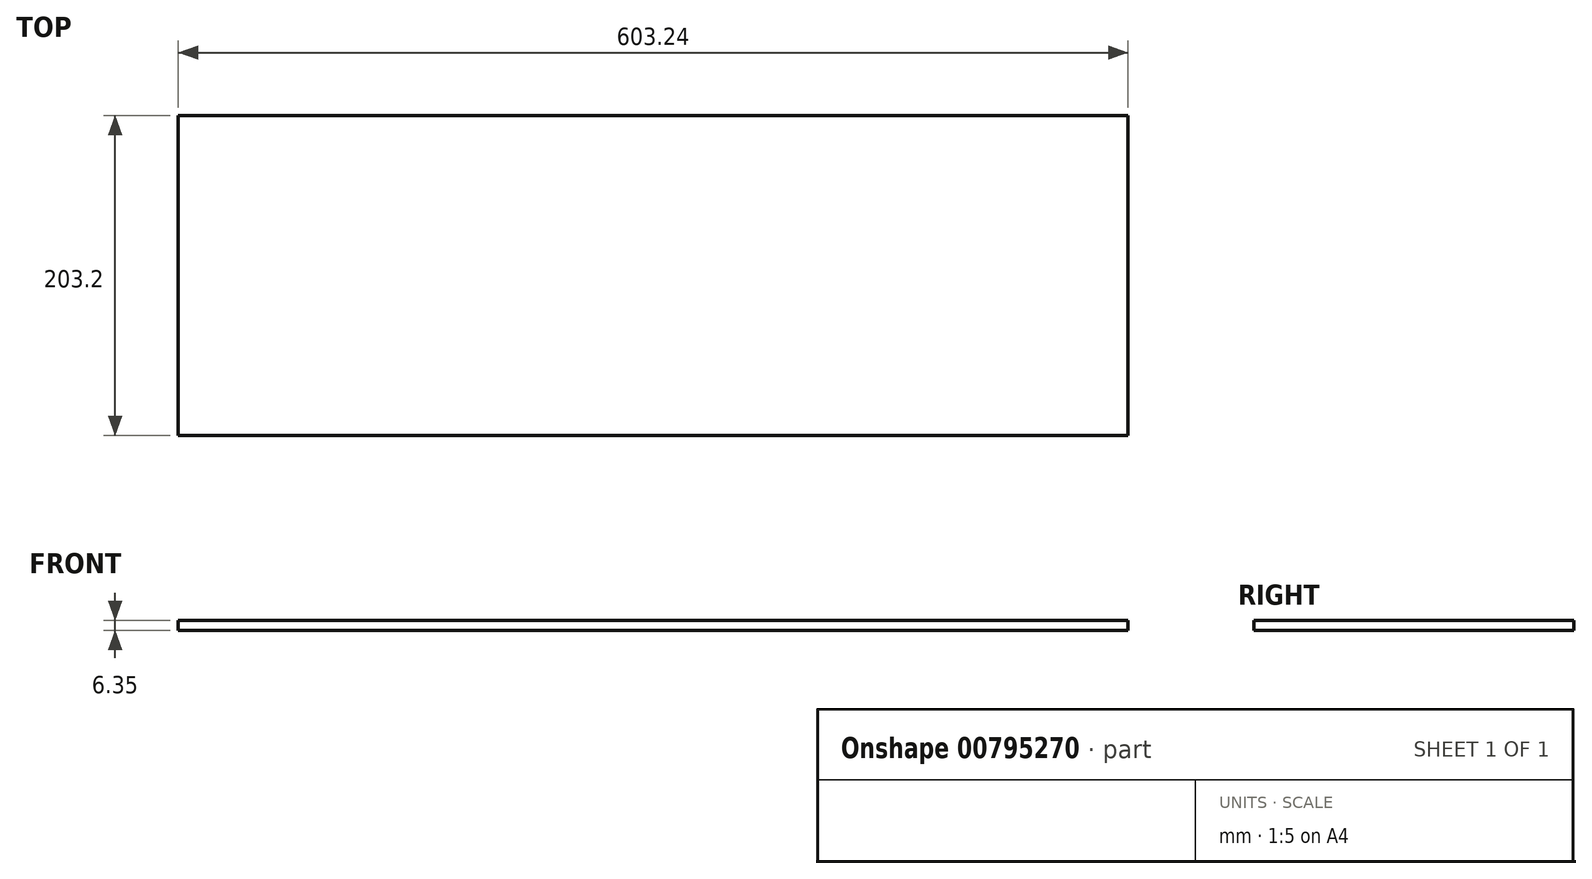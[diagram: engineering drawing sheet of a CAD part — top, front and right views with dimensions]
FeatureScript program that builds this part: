
annotation { "Feature Type Name" : "Feature", "Feature Type Description" : "" }
export const myFeature = defineFeature(function(context is Context, id is Id, definition is map)
    precondition{}
    {
        {
            var Q0;
            Q0=qCreatedBy(makeId("Top.planeOp"),FACE);
            var sketch = newSketch(context, id + "F0", { "sketchPlane" : qUnion([Q0])});
            skLineSegment(sketch, "E0.bottom", {"start": v(301.62, -101.6) * mm, "end": v(-301.63, -101.6) * mm});
            skLineSegment(sketch, "E0.top", {"start": v(301.62, 101.6) * mm, "end": v(-301.63, 101.6) * mm});
            skLineSegment(sketch, "E0.left", {"start": v(301.62, -101.6) * mm, "end": v(301.62, 101.6) * mm});
            skLineSegment(sketch, "E0.right", {"start": v(-301.63, -101.6) * mm, "end": v(-301.63, 101.6) * mm});
            skPoint(sketch, "E0.middle", {"position": v(0, 0) * mm});
            skSolve(sketch);
        }
        {
            var Q0;
            Q0 = qSketchRegion(id + "F0", true);
            extrude(context, id + "F1", {"entities" : qUnion([Q0]), "depth" : 6.35 * mm, "offsetDistance" : 25.4 * mm});
        }
    });
